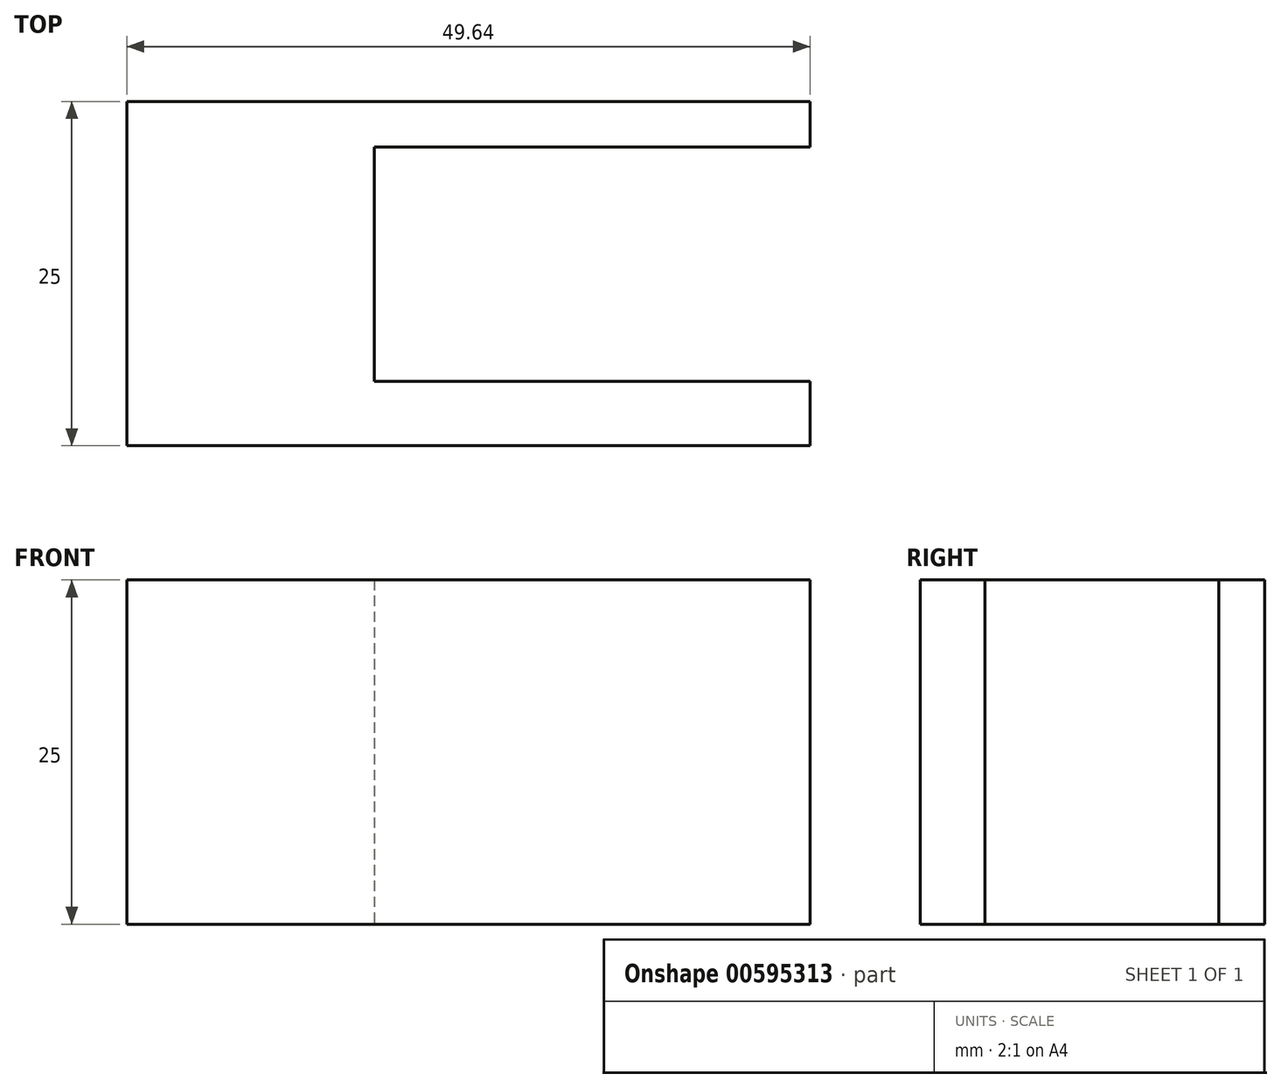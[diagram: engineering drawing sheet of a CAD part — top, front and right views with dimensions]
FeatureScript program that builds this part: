
annotation { "Feature Type Name" : "Feature", "Feature Type Description" : "" }
export const myFeature = defineFeature(function(context is Context, id is Id, definition is map)
    precondition{}
    {
        {
            var Q0;
            Q0=qCreatedBy(makeId("Top.planeOp"),FACE);
            var sketch = newSketch(context, id + "F0", { "sketchPlane" : qUnion([Q0])});
            skLineSegment(sketch, "E0.bottom", {"start": v(0, 0) * mm, "end": v(49.64, 0) * mm});
            skLineSegment(sketch, "E0.top", {"start": v(0, 25) * mm, "end": v(49.64, 25) * mm});
            skLineSegment(sketch, "E0.left", {"start": v(0, 0) * mm, "end": v(0, 25) * mm});
            skLineSegment(sketch, "E0.right", {"start": v(49.64, 0) * mm, "end": v(49.64, 4.68) * mm});
            skLineSegment(sketch, "E1.bottom", {"start": v(49.64, 21.68) * mm, "end": v(17.97, 21.68) * mm});
            skLineSegment(sketch, "E1.top", {"start": v(49.64, 4.68) * mm, "end": v(17.97, 4.68) * mm});
            skLineSegment(sketch, "E1.right", {"start": v(17.97, 21.68) * mm, "end": v(17.97, 4.68) * mm});
            skLineSegment(sketch, "E2.trimOffspring", {"start": v(49.64, 21.68) * mm, "end": v(49.64, 25) * mm});
            skSolve(sketch);
        }
        {
            var Q0;
            Q0=makeQuery(id+"F0.imprint","IMPRINT",FACE,{"disambiguationData":[TD([[makeQuery(id+"F0.imprint","IMPRINT",EDGE,{"derivedFrom":sQuery(id+"F0.wireOp",EDGE,"E0.bottom")}),1.0]])]});
            extrude(context, id + "F1", {"entities" : qUnion([Q0]), "depth" : 25 * mm, "offsetDistance" : 25 * mm});
        }
    });
